# Revit family: Приточная система с водяным нагревом фреоновым охлаждением
name_source: partatom
category: Оборудование
units: mm (PartAtom-declared; Revit-internal decimal feet)

## family parameters
Всегда вертикально = Да
Классификация = Нет
На основе рабочей плоскости = Нет
Общий = Нет
При загрузке вырезать с полостями = Нет
Размер круглого соединителя = Использовать диаметр
Тип детали = Нормальный
Точка принадлежности помещению = Нет

## types (17) — shared parameters
ADSK_Напряжение = 380 В
ADSK_Расход холодоносителя = 0.0 кубический метр в час
ADSK_Свободный напор воздуха = 400.0 Па
Длина гибкой встаки = 125 мм
Длина клапана FC = 120 мм
zero-valued in all types: Длина секции испарителя CF, Отметка по умолчанию

## per-type parameters (varying)
| type | ADSK_Масса | ADSK_Обозначение | ADSK_Размер_Высота | ADSK_Размер_Ширина | ADSK_Расход теплоносителя | ADSK_Частота вращения двигателя | Высота ГВ | Высота рамы | Коллектор испарителя вход | Коллектор испарителя выход | Подключение испарителя E | Слив конденсата | Ширина ГВ |
| 1А | 244 | П4.1 | 440 мм | 850 мм | 0.8 кубический метр в час | 2835 | 440 мм | 0 мм | 1 х 12мм | 1 х 16мм | 12 мм | 15 мм | 850 мм |
| 2А | 293 | П4.2 | 505 мм | 980 мм | 1.7 кубический метр в час | 2830 | 505 мм | 0 мм | 1 х 15мм | 1 х 22мм | 15 мм | 15 мм | 980 мм |
| 16B | 1862 | П4.16 | 2580 мм | 2580 мм | 23.2 кубический метр в час | 1460 | 2580 мм | 120 мм | 4 х 28мм | 4 х 35мм | 28 мм | 25 мм | 2580 мм |
| 3A | 347 | П4.3 | 695 мм | 1080 мм | 2.4 кубический метр в час | 2880 | 695 мм | 120 мм | 1 х 16мм | 1 х 22мм | 16 мм | 15 мм | 1080 мм |
| 4A | 402 | П4.4 | 695 мм | 1360 мм | 3.1 кубический метр в час | 2880 | 695 мм | 120 мм | 1 х 16мм | 1 х 22мм | 16 мм | 15 мм | 1360 мм |
| 5A | 436 | П4.5 | 803 мм | 1360 мм | 3.8 кубический метр в час | 2905 | 803 мм | 120 мм | 1 х 16мм | 1 х 22мм | 16 мм | 15 мм | 1360 мм |
| 6A | 525 | П4.6 | 803 мм | 1580 мм | 4.4 кубический метр в час | 1455 | 803 мм | 120 мм | 1 х 28мм | 1 х 35мм | 28 мм | 15 мм | 1580 мм |
| 7A | 561 | П4.7 | 990 мм | 1580 мм | 5.1 кубический метр в час | 2945 | 990 мм | 120 мм | 1 х 22мм | 1 х 28мм | 22 мм | 15 мм | 1580 мм |
| 8A | 663.3 | П4.8 | 990 мм | 1950 мм | 6.1 кубический метр в час | 1455 | 990 мм | 120 мм | 1 х 22мм | 1 х 28мм | 22 мм | 15 мм | 1950 мм |
| 9A | 768 | П4.9 | 1095 мм | 2160 мм | 8.2 кубический метр в час | 1460 | 1095 мм | 120 мм | 2 х 28мм | 2 х 42мм | 28 мм | 15 мм | 2160 мм |
| 10B | 934.5 | П4.10 | 1360 мм | 2040 мм | 9.6 кубический метр в час | 1465 | 1360 мм | 120 мм | 2 х 28мм | 2 х 35мм | 28 мм | 25 мм | 2040 мм |
| 12B | 1110 | П4.12 | 1680 мм | 2040 мм | 13.0 кубический метр в час | 1470 | 1680 мм | 120 мм | 2 х 28мм | 2 х 35мм | 20 мм | 15 мм | 2040 мм |
| 11B | 1105 | П4.11 | 1360 мм | 2580 мм | 10.9 кубический метр в час | 1465 | 1360 мм | 120 мм | 2 х 28мм | 2 х 35мм | 28 мм | 25 мм | 2580 мм |
| 13B | 1219 | П4.13 | 2040 мм | 2040 мм | 15.0 кубический метр в час | 1465 | 2040 мм | 120 мм | 3 х 28мм | 3 х 35мм | 28 мм | 25 мм | 2040 мм |
| 14B | 1307.5 | П4.14 | 1680 мм | 2580 мм | 19.8 кубический метр в час | 1460 | 1680 мм | 120 мм | 2 х 28мм | 2 х 35мм | 28 мм | 25 мм | 2580 мм |
| 15B | 1528 | П4.15 | 2040 мм | 2580 мм | 21.2 кубический метр в час | 1470 | 2040 мм | 120 мм | 3 х 28мм | 3 х 35мм | 28 мм | 25 мм | 2580 мм |
| 13В | 1369 | П4.13 | 2040 мм | 2040 мм | 17.1 кубический метр в час | 975 | 2040 мм | 120 мм | 3 х 28мм | 3 х 35мм | 28 мм | 25 мм | 2040 мм |
